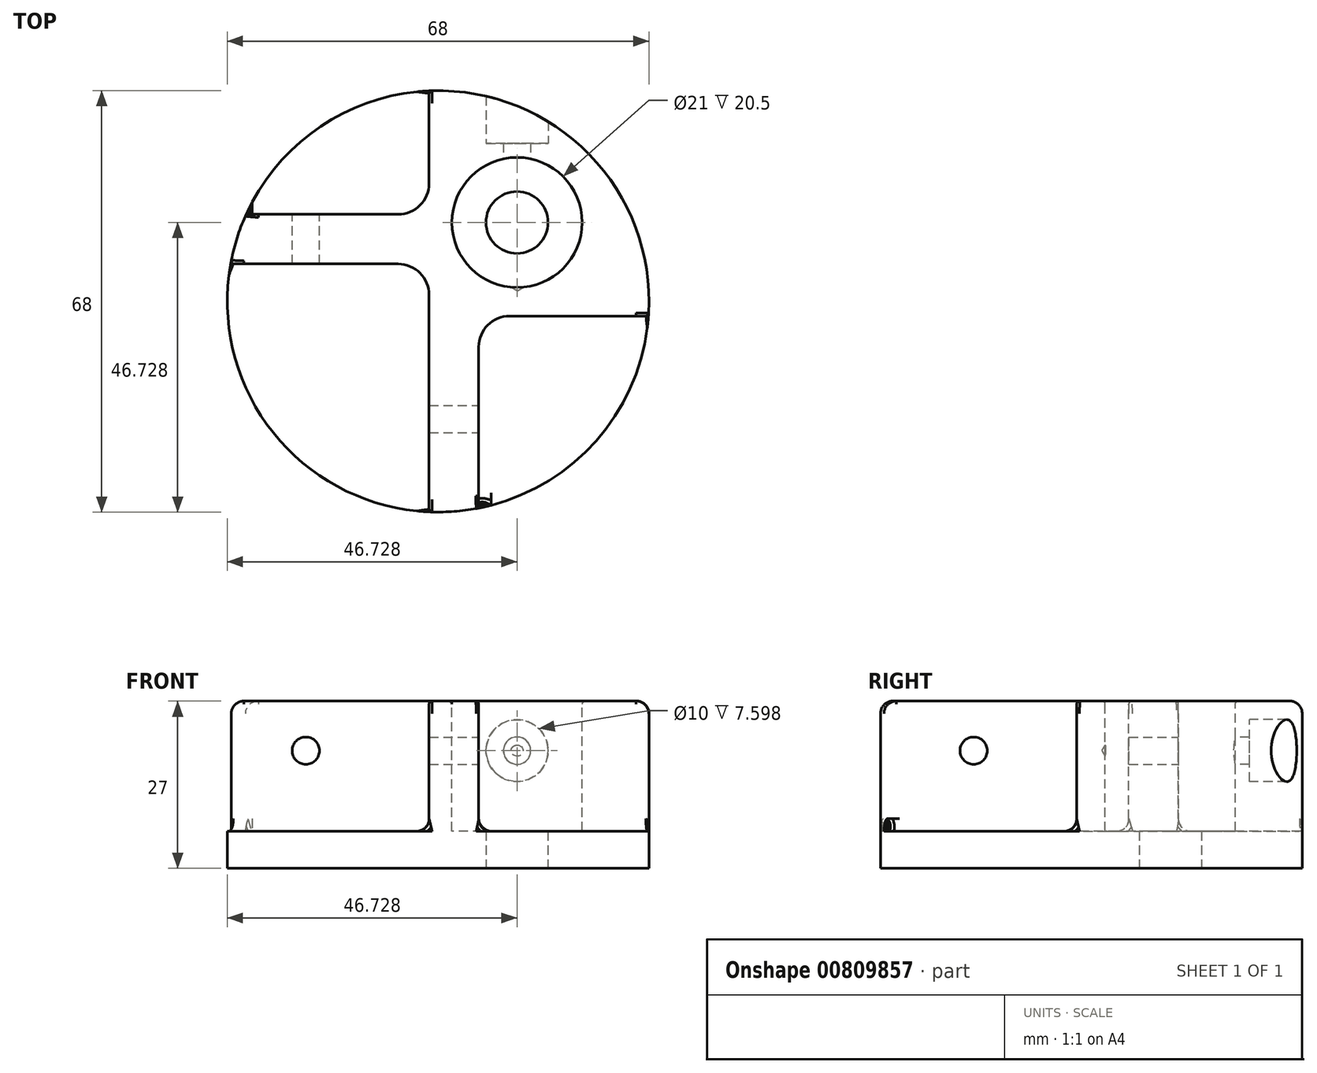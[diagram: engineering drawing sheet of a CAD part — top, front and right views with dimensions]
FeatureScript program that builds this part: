
annotation { "Feature Type Name" : "Feature", "Feature Type Description" : "" }
export const myFeature = defineFeature(function(context is Context, id is Id, definition is map)
    precondition{}
    {
        {
            var Q0;
            Q0=qCreatedBy(makeId("Top.planeOp"),FACE);
            var sketch = newSketch(context, id + "F0", { "sketchPlane" : qUnion([Q0])});
            skCircle(sketch, "E0", {"center": v(0, 0) * mm, "radius": 34 * mm});
            skSolve(sketch);
        }
        {
            var Q0;
            Q0 = qSketchRegion(id + "F0", true);
            extrude(context, id + "F1", {"entities" : qUnion([Q0]), "depth" : 27 * mm, "offsetDistance" : 25 * mm});
        }
        {
            var Q0;
            Q0=makeQuery(id+"F1.opExtrude","CAP_FACE",FACE,{"disambiguationData":[OSD([sQuery(id+"F0.wireOp",EDGE,"E0")])],"isStart":false});
            var sketch = newSketch(context, id + "F2", { "sketchPlane" : qUnion([Q0])});
            skLineSegment(sketch, "E1", {"start": v(-33.46, 6.03) * mm, "end": v(-6.46, 6.03) * mm});
            skLineSegment(sketch, "E2", {"start": v(-1.46, -33.97) * mm, "end": v(-1.46, 1.03) * mm});
            skPoint(sketch, "E3.visualSharp", {"position": v(-1.46, 6.03) * mm});
            skArc(sketch, "E3.filletArc", {"start": v(-1.46, 1.03) * mm, "mid": v(-2.93, 4.57) * mm, "end": v(-6.46, 6.03) * mm});
            skLineSegment(sketch, "E4", {"start": v(-30.97, 14.03) * mm, "end": v(-6.46, 14.03) * mm});
            skLineSegment(sketch, "E5", {"start": v(-1.46, 19.03) * mm, "end": v(-1.46, 33.97) * mm});
            skPoint(sketch, "E6.visualSharp", {"position": v(-1.46, 14.03) * mm});
            skArc(sketch, "E6.filletArc", {"start": v(-6.46, 14.03) * mm, "mid": v(-2.93, 15.5) * mm, "end": v(-1.46, 19.03) * mm});
            skLineSegment(sketch, "E7", {"start": v(6.54, -33.37) * mm, "end": v(6.54, -7.37) * mm});
            skLineSegment(sketch, "E8", {"start": v(11.54, -2.37) * mm, "end": v(33.92, -2.37) * mm});
            skPoint(sketch, "E9.visualSharp", {"position": v(6.54, -2.37) * mm});
            skArc(sketch, "E9.filletArc", {"start": v(11.54, -2.37) * mm, "mid": v(8, -3.83) * mm, "end": v(6.54, -7.37) * mm});
            skLineSegment(sketch, "E10", {"start": v(0, 0) * mm, "end": v(24.04, 24.04) * mm});
            skPoint(sketch, "E11", {"position": v(12.73, 12.73) * mm});
            skCircle(sketch, "E12", {"center": v(12.73, 12.73) * mm, "radius": 10.5 * mm});
            skLineSegment(sketch, "E13", {"start": v(12.73, 12.73) * mm, "end": v(12.73, 31.53) * mm});
            skPoint(sketch, "E14", {"position": v(0, 33.97) * mm});
            skLineSegment(sketch, "E15", {"start": v(2.23, 12.73) * mm, "end": v(0, 12.73) * mm});
            skSolve(sketch);
        }
        {
            var Q0;
            Q0=makeQuery(id+"F1.opExtrude","CAP_EDGE",EDGE,{"disambiguationData":[OSD([sQuery(id+"F0.wireOp",EDGE,"E0")])],"isStart":false});
            fillet(context, id + "F3", {"entities" : qUnion([Q0]), "radius" : 2 * mm, "tangentPropagation" : true, "allowEdgeOverflow" : false});
        }
        {
            var Q0;
            {var subQ0=sQuery(id+"F2.wireOp",EDGE,"E4");Q0=makeQuery(id+"F2.imprint","IMPRINT",FACE,{"disambiguationData":[TD([[makeQuery(id+"F2.imprint","IMPRINT",EDGE,{"derivedFrom":subQ0}),1.0]])]});}
            var Q1;
            {var subQ0=sQuery(id+"F2.wireOp",EDGE,"E1");Q1=makeQuery(id+"F2.imprint","IMPRINT",FACE,{"disambiguationData":[TD([[makeQuery(id+"F2.imprint","IMPRINT",EDGE,{"derivedFrom":subQ0}),-1.0]])]});}
            var Q2;
            {var subQ0=sQuery(id+"F2.wireOp",EDGE,"E7");Q2=makeQuery(id+"F2.imprint","IMPRINT",FACE,{"disambiguationData":[TD([[makeQuery(id+"F2.imprint","IMPRINT",EDGE,{"derivedFrom":subQ0}),-1.0]])]});}
            var Q3;
            {var subQ0=sQuery(id+"F2.wireOp",EDGE,"E12");var subQ1=sQuery(id+"F2.wireOp",EDGE,"E10");var subQ2=makeQuery(id+"F2.imprint","INTERSECT",VERTEX,{"disambiguationData":[OD(0.0)],"derivedFrom":[subQ1,subQ0]});Q3=makeQuery(id+"F2.imprint","IMPRINT",FACE,{"disambiguationData":[TD([[makeQuery(id+"F2.imprint","IMPRINT",EDGE,{"disambiguationData":[TD([[subQ2,-1.0]])],"derivedFrom":subQ1}),1.0]])]});}
            var Q4;
            {var subQ0=sQuery(id+"F2.wireOp",EDGE,"E12");var subQ1=sQuery(id+"F2.wireOp",EDGE,"E10");var subQ2=makeQuery(id+"F2.imprint","INTERSECT",VERTEX,{"disambiguationData":[OD(0.0)],"derivedFrom":[subQ1,subQ0]});Q4=makeQuery(id+"F2.imprint","IMPRINT",FACE,{"disambiguationData":[TD([[makeQuery(id+"F2.imprint","IMPRINT",EDGE,{"disambiguationData":[TD([[subQ2,-1.0]])],"derivedFrom":subQ1}),-1.0]])]});}
            var Q5;
            {var subQ0=sQuery(id+"F2.wireOp",EDGE,"E13");var subQ1=sQuery(id+"F2.wireOp",EDGE,"E10");var subQ2=makeQuery(id+"F2.imprint","INTERSECT",VERTEX,{"derivedFrom":[subQ1,subQ0]});Q5=makeQuery(id+"F2.imprint","IMPRINT",FACE,{"disambiguationData":[TD([[makeQuery(id+"F2.imprint","IMPRINT",EDGE,{"disambiguationData":[TD([[subQ2,-1.0]])],"derivedFrom":subQ1}),1.0]])]});}
            extrude(context, id + "F4", {"entities" : qUnion([Q0, Q1, Q2, Q3, Q4, Q5]), "operationType" : NewBodyOperationType.REMOVE, "oppositeDirection" : true, "depth" : 21 * mm, "offsetDistance" : 25 * mm});
        }
        {
            var Q0;
            Q0=makeQuery(id+"F4.boolean.opBoolean","COPY",EDGE,{"derivedFrom":makeQuery(id+"F4.opExtrude","CAP_EDGE",EDGE,{"disambiguationData":[OSD([sQuery(id+"F2.wireOp",EDGE,"E12")])],"isStart":true})});
            var Q1;
            Q1=makeQuery(id+"F1.opExtrude","CAP_FACE",FACE,{"disambiguationData":[OSD([sQuery(id+"F0.wireOp",EDGE,"E0")])],"isStart":false});
            fillet(context, id + "F5", {"entities" : qUnion([Q0, Q1]), "radius" : 0.5 * mm, "tangentPropagation" : true, "allowEdgeOverflow" : false});
        }
        {
            var Q0;
            Q0=makeQuery(id+"F1.opExtrude","CAP_FACE",FACE,{"disambiguationData":[OSD([sQuery(id+"F0.wireOp",EDGE,"E0")])],"isStart":true});
            var sketch = newSketch(context, id + "F6", { "sketchPlane" : qUnion([Q0])});
            skPoint(sketch, "E16", {"position": v(12.72, -12.73) * mm});
            skCircle(sketch, "E17", {"center": v(12.72, -12.73) * mm, "radius": 5 * mm});
            skSolve(sketch);
        }
        {
            var Q0;
            Q0=makeQuery(id+"F6.imprint","IMPRINT",FACE,{"disambiguationData":[TD([[makeQuery(id+"F6.imprint","IMPRINT",EDGE,{"derivedFrom":sQuery(id+"F6.wireOp",EDGE,"E17")}),1.0]])]});
            extrude(context, id + "F7", {"entities" : qUnion([Q0]), "operationType" : NewBodyOperationType.REMOVE, "oppositeDirection" : true, "depth" : 7 * mm, "offsetDistance" : 25 * mm});
        }
        {
            var Q0;
            Q0=makeQuery(id+"F4.boolean.opBoolean","COPY",FACE,{"derivedFrom":makeQuery(id+"F4.opExtrude","SWEPT_FACE",FACE,{"disambiguationData":[OSD([sQuery(id+"F2.wireOp",EDGE,"E2")])]})});
            var sketch = newSketch(context, id + "F8", { "sketchPlane" : qUnion([Q0])});
            skPoint(sketch, "E18", {"position": v(18.99, 19) * mm});
            skSolve(sketch);
        }
        {
            var Q0;
            Q0=sQuery(id+"F8.wireOp",VERTEX,"E18");
            var Q1;
            Q1=makeQuery(id+"F1.opExtrude","SWEPT_BODY",BODY,{"disambiguationData":[OSD([sQuery(id+"F0.wireOp",EDGE,"E0")])]});
            hole(context, id + "F9", {"style" : HoleStyle.SIMPLE, "endStyle" : HoleEndStyle.BLIND, "standardTappedOrClearance" : lookupTablePath({ "standard" : "ISO", "fit" : "Normal", "size" : "M4", "type" : "Clearance" }), "standardBlindInLast" : lookupTablePath({ "fit" : "Standard", "standard" : "ISO", "size" : "M4", "type" : "Clearance" }), "holeDiameter" : 4.4 * mm, "majorDiameter" : 5 * mm, "holeDepth" : 10 * mm, "isTappedThrough" : true, "tappedDepth" : 12 * mm, "tapClearance" : 3, "locations" : qUnion([Q0]), "scope" : qUnion([Q1])});
        }
        {
            var Q0;
            Q0=makeQuery(id+"F4.boolean.opBoolean","COPY",FACE,{"derivedFrom":makeQuery(id+"F4.opExtrude","SWEPT_FACE",FACE,{"disambiguationData":[OSD([sQuery(id+"F2.wireOp",EDGE,"E1")])]})});
            var sketch = newSketch(context, id + "F10", { "sketchPlane" : qUnion([Q0])});
            skPoint(sketch, "E19", {"position": v(-21.35, 19) * mm});
            skSolve(sketch);
        }
        {
            var Q0;
            Q0=sQuery(id+"F10.wireOp",VERTEX,"E19");
            var Q1;
            Q1=makeQuery(id+"F1.opExtrude","SWEPT_BODY",BODY,{"disambiguationData":[OSD([sQuery(id+"F0.wireOp",EDGE,"E0")])]});
            hole(context, id + "F11", {"style" : HoleStyle.SIMPLE, "endStyle" : HoleEndStyle.BLIND, "standardTappedOrClearance" : lookupTablePath({ "standard" : "ISO", "fit" : "Normal", "size" : "M4", "type" : "Clearance" }), "standardBlindInLast" : lookupTablePath({ "fit" : "Standard", "standard" : "ISO", "size" : "M4", "type" : "Clearance" }), "holeDiameter" : 4.4 * mm, "majorDiameter" : 5 * mm, "holeDepth" : 10 * mm, "isTappedThrough" : true, "tappedDepth" : 12 * mm, "tapClearance" : 3, "locations" : qUnion([Q0]), "scope" : qUnion([Q1])});
        }
        {
            var Q0;
            Q0=qCreatedBy(makeId("Front.planeOp"),FACE);
            cPlane(context, id + "F12", {"entities" : qUnion([Q0]), "cplaneType" : CPlaneType.OFFSET, "offset" : 34 * mm, "oppositeDirection" : true, "width" : 150 * mm, "height" : 150 * mm});
        }
        {
            var Q0;
            Q0=qCreatedBy(id+"F12.planeOp",FACE);
            var sketch = newSketch(context, id + "F13", { "sketchPlane" : qUnion([Q0])});
            skPoint(sketch, "E20", {"position": v(12.73, 19) * mm});
            skSolve(sketch);
        }
        {
            var Q0;
            Q0=sQuery(id+"F13.wireOp",VERTEX,"E20");
            var Q1;
            Q1=makeQuery(id+"F1.opExtrude","SWEPT_BODY",BODY,{"disambiguationData":[OSD([sQuery(id+"F0.wireOp",EDGE,"E0")])]});
            hole(context, id + "F14", {"style" : HoleStyle.C_BORE, "endStyle" : HoleEndStyle.BLIND, "oppositeDirection" : true, "holeDiameter" : 4.4 * mm, "cBoreDiameter" : 10 * mm, "cBoreDepth" : 3.5 * mm, "majorDiameter" : 5 * mm, "holeDepth" : 26 * mm, "isTappedThrough" : true, "tappedDepth" : 12 * mm, "tapClearance" : 3, "locations" : qUnion([Q0]), "scope" : qUnion([Q1])});
        }
        {
            var Q0;
            Q0=makeQuery(id+"F1.opExtrude","SWEPT_BODY",BODY,{"disambiguationData":[OSD([sQuery(id+"F0.wireOp",EDGE,"E0")])]});
            transform(context, id + "F15", {"entities" : qUnion([Q0]), "transformType" : TransformType.TRANSLATION_3D, "dx" : 0 * mm, "dy" : 0 * mm, "dz" : 0 * mm, "makeCopy" : true});
        }
        {
            var Q0;
            Q0=makeQuery(id+"F1.opExtrude","SWEPT_BODY",BODY,{"disambiguationData":[OSD([sQuery(id+"F0.wireOp",EDGE,"E0")])]});
            transform(context, id + "F16", {"entities" : qUnion([Q0]), "transformType" : TransformType.TRANSLATION_3D, "dx" : 0 * mm, "dy" : 0 * mm, "dz" : 0 * mm, "makeCopy" : true});
        }
        {
            var Q0;
            Q0=makeQuery(id+"F15.opPattern","COPY",BODY,{"derivedFrom":makeQuery(id+"F1.opExtrude","SWEPT_BODY",BODY,{"disambiguationData":[OSD([sQuery(id+"F0.wireOp",EDGE,"E0")])]}),"instanceName":"1"});
            deleteBodies(context, id + "F17", {"entities" : qUnion([Q0])});
        }
        {
            var Q0;
            Q0=makeQuery(id+"F16.opPattern","COPY",BODY,{"derivedFrom":makeQuery(id+"F1.opExtrude","SWEPT_BODY",BODY,{"disambiguationData":[OSD([sQuery(id+"F0.wireOp",EDGE,"E0")])]}),"instanceName":"1"});
            deleteBodies(context, id + "F18", {"entities" : qUnion([Q0])});
        }
        {
            var Q0;
            Q0=makeQuery(id+"F4.boolean.opBoolean","COPY",EDGE,{"derivedFrom":makeQuery(id+"F4.opExtrude","CAP_EDGE",EDGE,{"disambiguationData":[OSD([sQuery(id+"F2.wireOp",EDGE,"E8")])],"isStart":false})});
            var Q1;
            Q1=makeQuery(id+"F4.boolean.opBoolean","COPY",EDGE,{"derivedFrom":makeQuery(id+"F4.opExtrude","CAP_EDGE",EDGE,{"disambiguationData":[OSD([sQuery(id+"F2.wireOp",EDGE,"E9.filletArc")])],"isStart":false})});
            var Q2;
            Q2=makeQuery(id+"F4.boolean.opBoolean","COPY",EDGE,{"derivedFrom":makeQuery(id+"F4.opExtrude","CAP_EDGE",EDGE,{"disambiguationData":[OSD([sQuery(id+"F2.wireOp",EDGE,"E7")])],"isStart":false})});
            var Q3;
            Q3=makeQuery(id+"F4.boolean.opBoolean","COPY",EDGE,{"derivedFrom":makeQuery(id+"F4.opExtrude","CAP_EDGE",EDGE,{"disambiguationData":[OSD([sQuery(id+"F2.wireOp",EDGE,"E2")])],"isStart":false})});
            var Q4;
            Q4=makeQuery(id+"F4.boolean.opBoolean","COPY",EDGE,{"derivedFrom":makeQuery(id+"F4.opExtrude","CAP_EDGE",EDGE,{"disambiguationData":[OSD([sQuery(id+"F2.wireOp",EDGE,"E3.filletArc")])],"isStart":false})});
            var Q5;
            Q5=makeQuery(id+"F4.boolean.opBoolean","COPY",EDGE,{"derivedFrom":makeQuery(id+"F4.opExtrude","CAP_EDGE",EDGE,{"disambiguationData":[OSD([sQuery(id+"F2.wireOp",EDGE,"E1")])],"isStart":false})});
            var Q6;
            Q6=makeQuery(id+"F4.boolean.opBoolean","COPY",EDGE,{"derivedFrom":makeQuery(id+"F4.opExtrude","CAP_EDGE",EDGE,{"disambiguationData":[OSD([sQuery(id+"F2.wireOp",EDGE,"E4")])],"isStart":false})});
            var Q7;
            Q7=makeQuery(id+"F4.boolean.opBoolean","COPY",EDGE,{"derivedFrom":makeQuery(id+"F4.opExtrude","CAP_EDGE",EDGE,{"disambiguationData":[OSD([sQuery(id+"F2.wireOp",EDGE,"E6.filletArc")])],"isStart":false})});
            var Q8;
            Q8=makeQuery(id+"F4.boolean.opBoolean","COPY",EDGE,{"derivedFrom":makeQuery(id+"F4.opExtrude","CAP_EDGE",EDGE,{"disambiguationData":[OSD([sQuery(id+"F2.wireOp",EDGE,"E5")])],"isStart":false})});
            fillet(context, id + "F19", {"entities" : qUnion([Q0, Q1, Q2, Q3, Q4, Q5, Q6, Q7, Q8]), "radius" : 2 * mm, "tangentPropagation" : true, "allowEdgeOverflow" : false});
        }
    });
